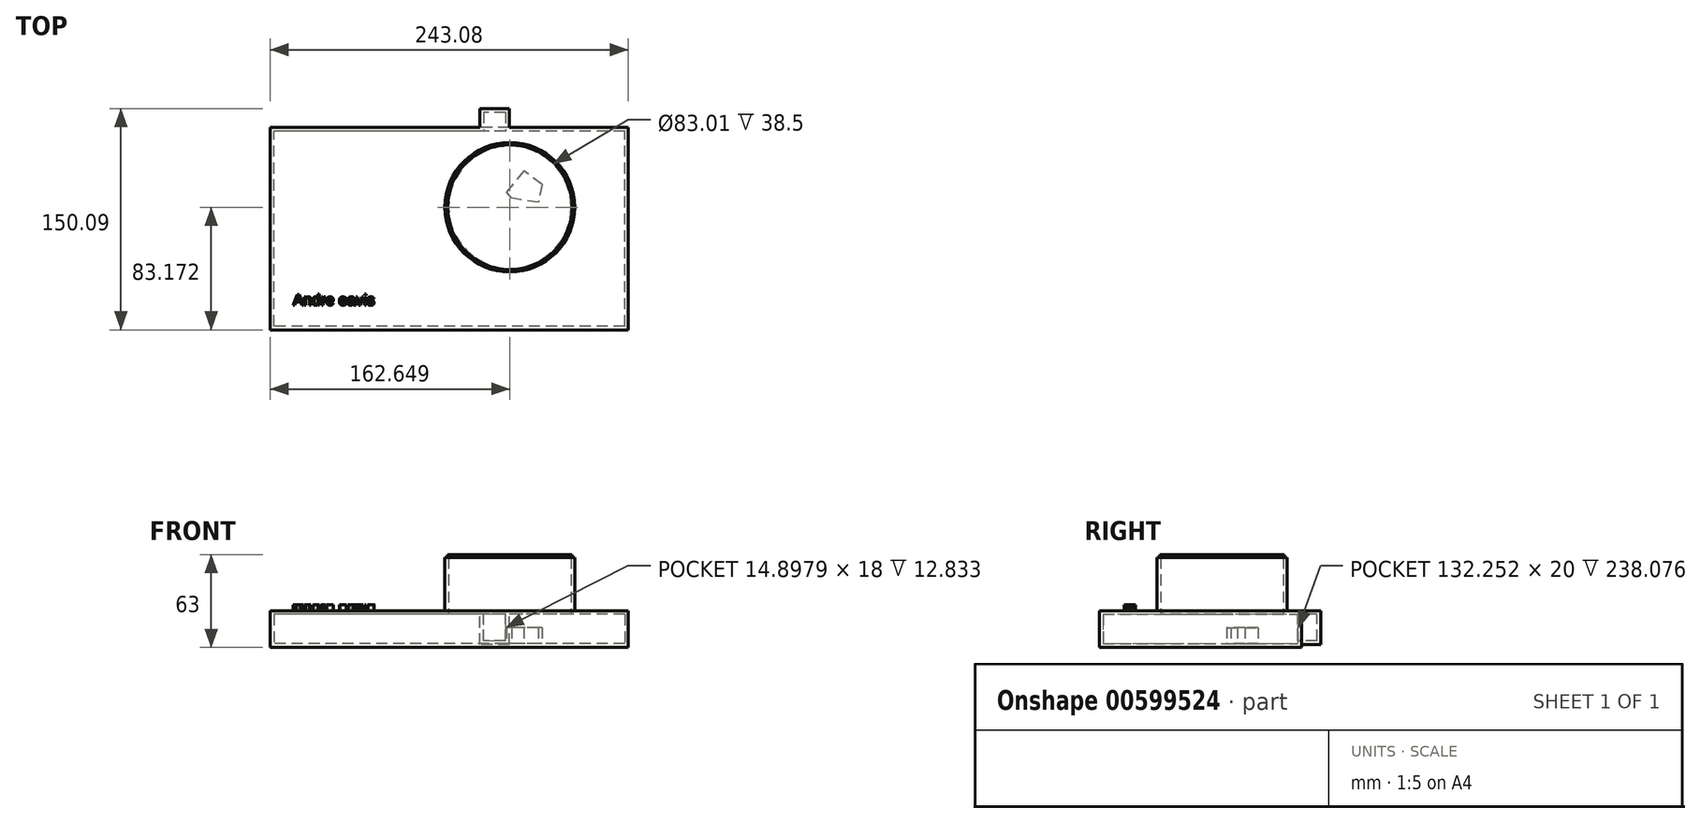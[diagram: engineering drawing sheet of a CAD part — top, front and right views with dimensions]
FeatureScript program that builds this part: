
annotation { "Feature Type Name" : "Feature", "Feature Type Description" : "" }
export const myFeature = defineFeature(function(context is Context, id is Id, definition is map)
    precondition{}
    {
        {
            var Q0;
            Q0=qCreatedBy(makeId("Top.planeOp"),FACE);
            var sketch = newSketch(context, id + "F0", { "sketchPlane" : qUnion([Q0])});
            skLineSegment(sketch, "E0.bottom", {"start": v(121.54, -68.63) * mm, "end": v(-121.54, -68.63) * mm});
            skLineSegment(sketch, "E0.top", {"start": v(121.54, 68.63) * mm, "end": v(-121.54, 68.63) * mm});
            skLineSegment(sketch, "E0.left", {"start": v(121.54, -68.63) * mm, "end": v(121.54, 68.63) * mm});
            skLineSegment(sketch, "E0.right", {"start": v(-121.54, -68.63) * mm, "end": v(-121.54, 68.63) * mm});
            skPoint(sketch, "E0.middle", {"position": v(0, 0) * mm});
            skSolve(sketch);
        }
        {
            var Q0;
            Q0=makeQuery(id+"F0.imprint","IMPRINT",FACE,{"disambiguationData":[TD([[makeQuery(id+"F0.imprint","IMPRINT",EDGE,{"derivedFrom":sQuery(id+"F0.wireOp",EDGE,"E0.bottom")}),-1.0]])]});
            extrude(context, id + "F1", {"entities" : qUnion([Q0]), "depth" : 25 * mm, "offsetDistance" : 25 * mm});
        }
        {
            var Q0;
            Q0=makeQuery(id+"F1.opExtrude","CAP_FACE",FACE,{"disambiguationData":[OSD([sQuery(id+"F0.wireOp",EDGE,"E0.bottom"),sQuery(id+"F0.wireOp",EDGE,"E0.top"),sQuery(id+"F0.wireOp",EDGE,"E0.left"),sQuery(id+"F0.wireOp",EDGE,"E0.right")])],"isStart":false});
            var sketch = newSketch(context, id + "F2", { "sketchPlane" : qUnion([Q0])});
            skLineSegment(sketch, "E1.bottom", {"start": v(40.73, 81.46) * mm, "end": v(20.84, 81.46) * mm});
            skLineSegment(sketch, "E1.top", {"start": v(40.73, 67.56) * mm, "end": v(20.84, 67.56) * mm});
            skLineSegment(sketch, "E1.left", {"start": v(40.73, 81.46) * mm, "end": v(40.73, 67.56) * mm});
            skLineSegment(sketch, "E1.right", {"start": v(20.84, 81.46) * mm, "end": v(20.84, 67.56) * mm});
            skPoint(sketch, "E1.middle", {"position": v(30.78, 74.5) * mm});
            skSolve(sketch);
        }
        {
            var Q0;
            {var subQ0=sQuery(id+"F2.wireOp",EDGE,"E1.bottom");Q0=makeQuery(id+"F2.imprint","IMPRINT",FACE,{"disambiguationData":[TD([[makeQuery(id+"F2.imprint","IMPRINT",EDGE,{"derivedFrom":subQ0}),1.0]])]});}
            extrude(context, id + "F3", {"entities" : qUnion([Q0]), "operationType" : NewBodyOperationType.ADD, "oppositeDirection" : true, "depth" : 23 * mm, "offsetDistance" : 25 * mm});
        }
        {
            var Q0;
            {var subQ0=sQuery(id+"F0.wireOp",EDGE,"E0.top");Q0=makeQuery(id+"F3.boolean.opBoolean","MERGE",FACE,{"derivedFrom":[makeQuery(id+"F1.opExtrude","CAP_FACE",FACE,{"disambiguationData":[OSD([sQuery(id+"F0.wireOp",EDGE,"E0.bottom"),subQ0,sQuery(id+"F0.wireOp",EDGE,"E0.left"),sQuery(id+"F0.wireOp",EDGE,"E0.right")])],"isStart":false}),makeQuery(id+"F3.opExtrude","CAP_FACE",FACE,{"disambiguationData":[OSD([subQ0,sQuery(id+"F2.wireOp",EDGE,"E1.bottom"),sQuery(id+"F2.wireOp",EDGE,"E1.left"),sQuery(id+"F2.wireOp",EDGE,"E1.right")])],"isStart":true})]});}
            var sketch = newSketch(context, id + "F4", { "sketchPlane" : qUnion([Q0])});
            skCircle(sketch, "E2", {"center": v(41.1, 14.54) * mm, "radius": 44 * mm});
            skSolve(sketch);
        }
        {
            var Q0;
            Q0 = qSketchRegion(id + "F4", true);
            extrude(context, id + "F5", {"entities" : qUnion([Q0]), "operationType" : NewBodyOperationType.ADD, "depth" : 36 * mm, "offsetDistance" : 25 * mm});
        }
        {
            var Q0;
            Q0=makeQuery(id+"F5.opExtrude","CAP_FACE",FACE,{"disambiguationData":[OSD([sQuery(id+"F4.wireOp",EDGE,"E2")])],"isStart":false});
            shell(context, id + "F6", {"entities" : qUnion([Q0]), "thickness" : 2.5 * mm});
        }
        {
            var Q0;
            Q0=makeQuery(id+"F6.opShell","OFFSET_FACE",FACE,{"disambiguationData":[OSD([sQuery(id+"F0.wireOp",EDGE,"E0.bottom"),sQuery(id+"F0.wireOp",EDGE,"E0.top"),sQuery(id+"F0.wireOp",EDGE,"E0.left"),sQuery(id+"F0.wireOp",EDGE,"E0.right")])]});
            var sketch = newSketch(context, id + "F7", { "sketchPlane" : qUnion([Q0])});
            skLineSegment(sketch, "E3", {"start": v(28.24, 49.01) * mm, "end": v(28.24, 24.39) * mm});
            skLineSegment(sketch, "E4", {"start": v(48.07, 50.53) * mm, "end": v(21.64, 33.52) * mm});
            skLineSegment(sketch, "E5", {"start": v(39.44, 50.53) * mm, "end": v(66.75, 38.59) * mm});
            skLineSegment(sketch, "E6", {"start": v(66.75, 47.5) * mm, "end": v(60.22, 16.73) * mm});
            skLineSegment(sketch, "E7", {"start": v(66.75, 16.73) * mm, "end": v(20.08, 24.39) * mm});
            skLineSegment(sketch, "E8", {"start": v(48.07, 29.94) * mm, "end": v(43.25, 5.2) * mm});
            skLineSegment(sketch, "E9", {"start": v(54.95, 5.78) * mm, "end": v(21.64, 45.26) * mm});
            skLineSegment(sketch, "E10", {"start": v(60.22, 50.53) * mm, "end": v(28.24, 12.3) * mm});
            skLineSegment(sketch, "E11", {"start": v(70.66, 24.39) * mm, "end": v(28.24, 55.5) * mm});
            skSolve(sketch);
        }
        {
            var Q0;
            {var subQ0=sQuery(id+"F7.wireOp",EDGE,"E7");var subQ6=sQuery(id+"F7.wireOp",EDGE,"E6");var subQ7=makeQuery(id+"F7.imprint","INTERSECT",VERTEX,{"derivedFrom":[subQ6,subQ0]});Q0=makeQuery(id+"F7.imprint","IMPRINT",FACE,{"disambiguationData":[TD([[makeQuery(id+"F7.imprint","IMPRINT",EDGE,{"disambiguationData":[TD([[subQ7,1.0]])],"derivedFrom":subQ6}),-1.0]])]});}
            extrude(context, id + "F8", {"entities" : qUnion([Q0]), "operationType" : NewBodyOperationType.ADD, "depth" : 11 * mm, "offsetDistance" : 25 * mm});
        }
        {
            var Q0;
            Q0=makeQuery(id+"F5.opExtrude","CAP_FACE",FACE,{"disambiguationData":[OSD([sQuery(id+"F4.wireOp",EDGE,"E2")])],"isStart":false});
            var sketch = newSketch(context, id + "F9", { "sketchPlane" : qUnion([Q0])});
            skCircle(sketch, "E12", {"center": v(41.1, 14.54) * mm, "radius": 42.3 * mm});
            skSolve(sketch);
        }
        {
            var Q0;
            Q0 = qSketchRegion(id + "F9", true);
            extrude(context, id + "F10", {"entities" : qUnion([Q0]), "operationType" : NewBodyOperationType.ADD, "depth" : 2 * mm, "offsetDistance" : 25 * mm});
        }
        {
            var Q0;
            {var subQ0=sQuery(id+"F0.wireOp",EDGE,"E0.top");Q0=makeQuery(id+"F3.boolean.opBoolean","MERGE",FACE,{"derivedFrom":[makeQuery(id+"F1.opExtrude","CAP_FACE",FACE,{"disambiguationData":[OSD([sQuery(id+"F0.wireOp",EDGE,"E0.bottom"),subQ0,sQuery(id+"F0.wireOp",EDGE,"E0.left"),sQuery(id+"F0.wireOp",EDGE,"E0.right")])],"isStart":false}),makeQuery(id+"F3.opExtrude","CAP_FACE",FACE,{"disambiguationData":[OSD([subQ0,sQuery(id+"F2.wireOp",EDGE,"E1.bottom"),sQuery(id+"F2.wireOp",EDGE,"E1.left"),sQuery(id+"F2.wireOp",EDGE,"E1.right")])],"isStart":true})]});}
            var sketch = newSketch(context, id + "F11", { "sketchPlane" : qUnion([Q0])});
            skText(sketch, "E13", { "text": "Andre eavis", "fontName": "Arimo-Regular.ttf"});
            const initialGuessF11  = {"E13": [-0.10602, -0.05187, 1, 0, 0.00756]};
            skSetInitialGuess(sketch, initialGuessF11);
            skSolve(sketch);
        }
        {
            var Q0;
            Q0 = qSketchRegion(id + "F11", true);
            extrude(context, id + "F12", {"entities" : qUnion([Q0]), "operationType" : NewBodyOperationType.ADD, "depth" : 4 * mm, "offsetDistance" : 25 * mm});
        }
    });
